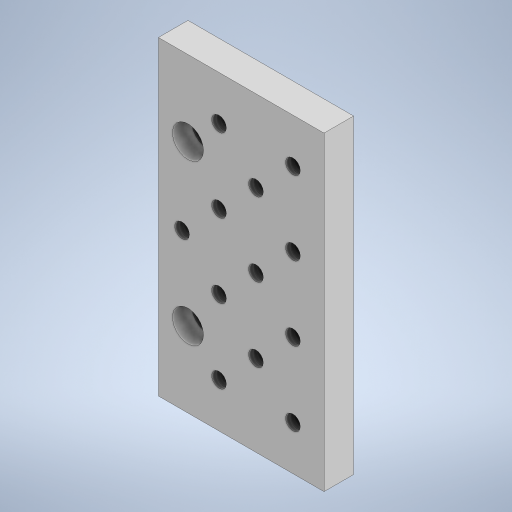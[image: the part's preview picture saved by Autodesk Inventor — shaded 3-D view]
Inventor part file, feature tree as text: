
AUTODESK INVENTOR PART (.ipt)
format: ipt  version: 2023 (Build 270158000, 158)  size: 285,696 bytes
history: native  units: in
note: dims shown in document units (in); Inventor stores cm internally (conversion verified against a paired STEP export)
features: sketch x3, hole x2, projected_geometry x2, extrude x1
ambient origin geometry x8: Origin, YZ Plane, XZ Plane, XY Plane, X Axis, Y Axis, Z Axis, Center Point
bodies: Solid1 (feature_tree)
feature tree (8):
  extrude  "Extrusion1"  Depth=2.2047in
  hole  "Hole1"  [1 undecoded]
  hole  "Hole2"  [1 undecoded]
  sketch  "Sketch1"  dims[d0=4.1339in d1=2.2047in]
  sketch  "Sketch2"  dims[d2=0.315in d3=0.3937in d4=0.0in]
  projected_geometry  "Projected Loop1"
  sketch  "Sketch3"  dims[d5=2.126in d6=0.3937in d7=0.2559in d8=0.75in d9=0.4134in d10=0.2559in d11=0.5635in d12=1.0in d13=0.8108in d14=0.9843in d15=0.9843in d16=0.9843in d17=0.4921in d18=0.4921in d19=0.9843in d20=0.4921in d21=0.9843in d22=0.196in d23=0.5in d24=0.4134in d25=0.2559in d26=0.5635in d27=1.0in d28=0.8108in d29=0.4921in d30=0.9843in d31=0.4921in d32=0.4921in d33=0.9843in]
  projected_geometry  "Projected Loop2"
note: 2 required parameter values undecoded (feature->parameter linkage not recoverable at this tier; creation-order binding heuristic only, values carry confidence <= 0.55)
